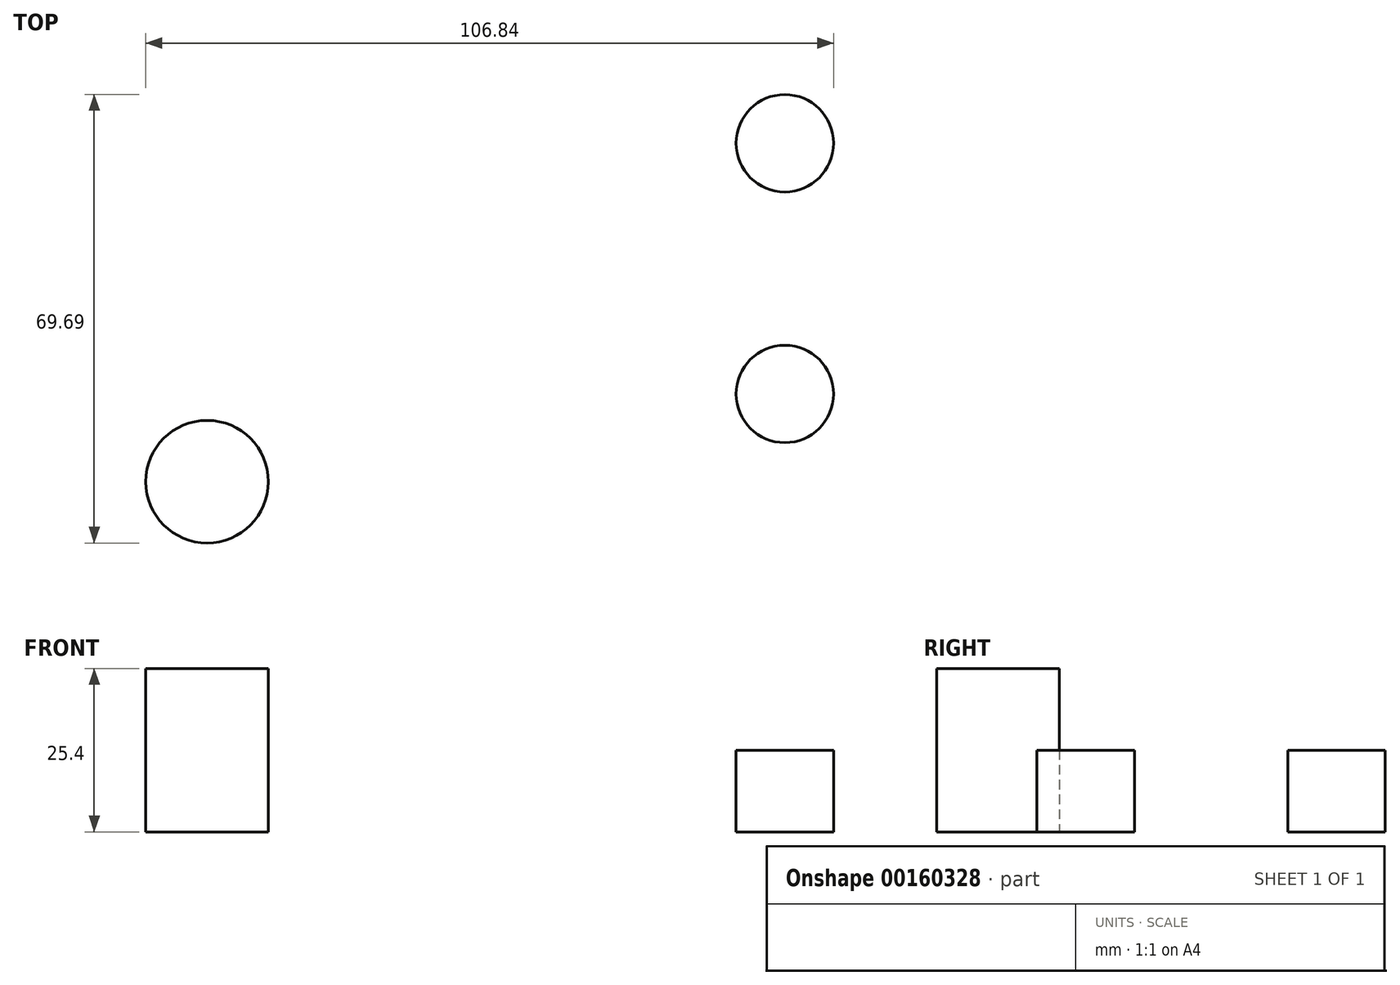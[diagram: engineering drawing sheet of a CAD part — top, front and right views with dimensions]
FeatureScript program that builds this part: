
annotation { "Feature Type Name" : "Feature", "Feature Type Description" : "" }
export const myFeature = defineFeature(function(context is Context, id is Id, definition is map)
    precondition{}
    {
        {
            var Q0;
            Q0=qCreatedBy(makeId("Top.planeOp"),FACE);
            var sketch = newSketch(context, id + "F0", { "sketchPlane" : qUnion([Q0])});
            skCircle(sketch, "E0", {"center": v(0, 0) * mm, "radius": 25.4 * mm});
            skCircle(sketch, "E1", {"center": v(0, 0) * mm, "radius": 38.1 * mm});
            skLineSegment(sketch, "E2", {"start": v(35.92, 12.7) * mm, "end": v(165.1, 12.7) * mm});
            skLineSegment(sketch, "E3", {"start": v(165.1, 12.7) * mm, "end": v(165.1, 38.1) * mm});
            skLineSegment(sketch, "E4", {"start": v(165.1, 38.1) * mm, "end": v(254, 38.1) * mm});
            skLineSegment(sketch, "E5", {"start": v(254, 38.1) * mm, "end": v(254, 25.4) * mm});
            skLineSegment(sketch, "E6", {"start": v(254, 25.4) * mm, "end": v(203.2, 25.4) * mm});
            skLineSegment(sketch, "E7", {"start": v(203.2, 25.4) * mm, "end": v(203.2, -25.4) * mm});
            skLineSegment(sketch, "E8", {"start": v(203.2, -25.4) * mm, "end": v(254, -25.4) * mm});
            skLineSegment(sketch, "E9", {"start": v(254, -25.4) * mm, "end": v(254, -38.1) * mm});
            skLineSegment(sketch, "E10", {"start": v(254, -38.1) * mm, "end": v(165.1, -38.1) * mm});
            skLineSegment(sketch, "E11", {"start": v(165.1, -38.1) * mm, "end": v(165.1, -12.7) * mm});
            skLineSegment(sketch, "E12", {"start": v(165.1, -12.7) * mm, "end": v(35.92, -12.7) * mm});
            skLineSegment(sketch, "E13", {"start": v(0, 0) * mm, "end": v(318.16, 0) * mm, "construction": true});
            skCircle(sketch, "E14", {"center": v(90.44, -33.12) * mm, "radius": 9.53 * mm});
            skSolve(sketch);
        }
        {
            var Q0;
            Q0 = qSketchRegion(id + "F0", true);
            extrude(context, id + "F1", {"entities" : qUnion([Q0]), "depth" : 25.4 * mm});
        }
        {
            var Q0;
            Q0=makeQuery(id+"F1.opExtrude","CAP_FACE",FACE,{"disambiguationData":[OSD([sQuery(id+"F0.wireOp",EDGE,"E0"),sQuery(id+"F0.wireOp",EDGE,"E1"),sQuery(id+"F0.wireOp",EDGE,"E2"),sQuery(id+"F0.wireOp",EDGE,"E3"),sQuery(id+"F0.wireOp",EDGE,"E4"),sQuery(id+"F0.wireOp",EDGE,"E5"),sQuery(id+"F0.wireOp",EDGE,"E6"),sQuery(id+"F0.wireOp",EDGE,"E7"),sQuery(id+"F0.wireOp",EDGE,"E8"),sQuery(id+"F0.wireOp",EDGE,"E9"),sQuery(id+"F0.wireOp",EDGE,"E10"),sQuery(id+"F0.wireOp",EDGE,"E11"),sQuery(id+"F0.wireOp",EDGE,"E12")])],"isStart":false});
            var sketch = newSketch(context, id + "F2", { "sketchPlane" : qUnion([Q0])});
            skCircle(sketch, "E15", {"center": v(180.19, 19.48) * mm, "radius": 7.57 * mm});
            skLineSegment(sketch, "E16", {"start": v(0, 0) * mm, "end": v(203.2, 0) * mm});
            skCircle(sketch, "E17.MirrorC", {"center": v(180.19, -19.48) * mm, "radius": 7.57 * mm});
            skSolve(sketch);
        }
        {
            var Q0;
            Q0=makeQuery(id+"F2.imprint","IMPRINT",FACE,{"disambiguationData":[TD([[makeQuery(id+"F2.imprint","IMPRINT",EDGE,{"derivedFrom":sQuery(id+"F2.wireOp",EDGE,"E17.MirrorC")}),-1.0]])]});
            extrude(context, id + "F3", {"entities" : qUnion([Q0]), "operationType" : NewBodyOperationType.REMOVE, "oppositeDirection" : true, "depth" : 25.4 * mm});
        }
        {
            var Q0;
            Q0 = qSketchRegion(id + "F2", true);
            var Q1;
            Q1=makeQuery(id+"F1.opExtrude","CAP_FACE",FACE,{"disambiguationData":[OSD([sQuery(id+"F0.wireOp",EDGE,"E0"),sQuery(id+"F0.wireOp",EDGE,"E1"),sQuery(id+"F0.wireOp",EDGE,"E2"),sQuery(id+"F0.wireOp",EDGE,"E3"),sQuery(id+"F0.wireOp",EDGE,"E4"),sQuery(id+"F0.wireOp",EDGE,"E5"),sQuery(id+"F0.wireOp",EDGE,"E6"),sQuery(id+"F0.wireOp",EDGE,"E7"),sQuery(id+"F0.wireOp",EDGE,"E8"),sQuery(id+"F0.wireOp",EDGE,"E9"),sQuery(id+"F0.wireOp",EDGE,"E10"),sQuery(id+"F0.wireOp",EDGE,"E11"),sQuery(id+"F0.wireOp",EDGE,"E12")])],"isStart":false});
            extrude(context, id + "F4", {"entities" : qUnion([Q0, Q1]), "operationType" : NewBodyOperationType.REMOVE, "endBound" : BoundingType.SYMMETRIC, "oppositeDirection" : true, "depth" : 25.4 * mm});
        }
    });
